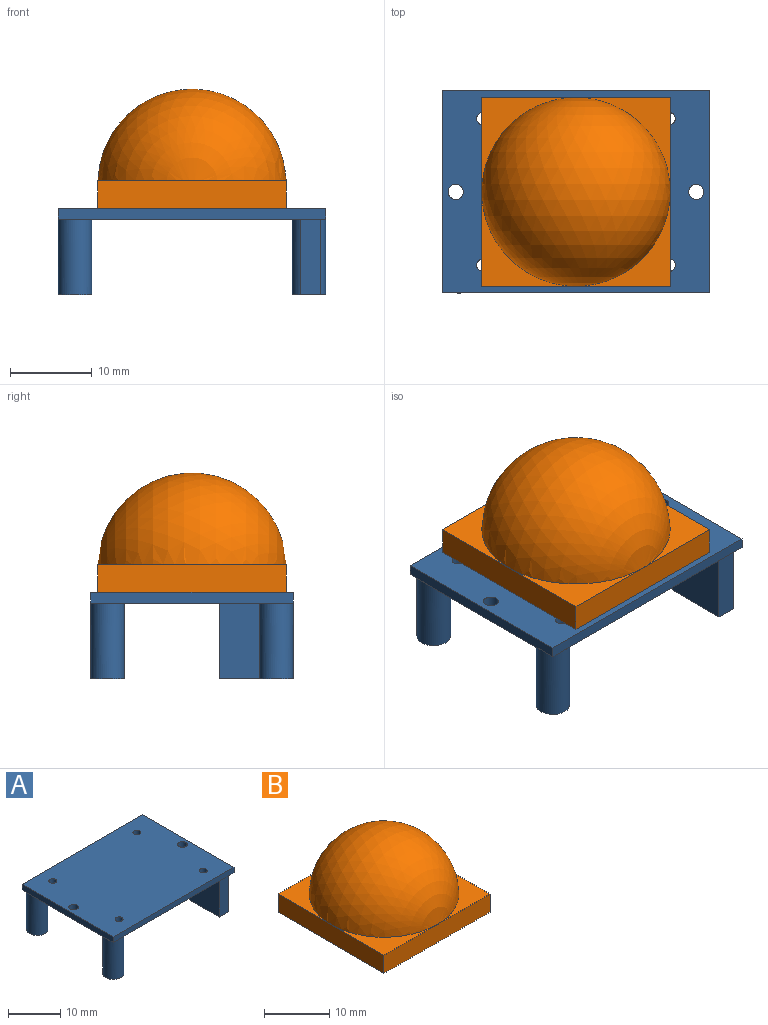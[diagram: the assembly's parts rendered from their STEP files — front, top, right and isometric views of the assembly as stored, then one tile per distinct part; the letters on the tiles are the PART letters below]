
ASSEMBLY  parts=2 mates=1
PART A: 26 faces, bbox 32.6x24.7x10.5 mm
  f0: plane 32.64x24.66mm, normal (0,0,-1), area 730mm2, adj f4,f5,f6,f7,f8,f9,f10,f11
  f1: plane 2.05x2.05mm, normal (0,0,-1), area 0.9mm2, adj f5,f6,f19
  f2: plane 2.05x2.05mm, normal (0,0,-1), area 0.9mm2, adj f6,f13,f17
  f3: plane 2.05x2.05mm, normal (0,0,-1), area 0.9mm2, adj f4,f13,f15
  f4: plane 32.64x1.3mm, normal (0,-1,0), area 42.4mm2, adj f0,f3,f5,f13,f14
  f5: plane 24.66x1.3mm, normal (1,0,0), area 32.1mm2, adj f0,f1,f4,f6,f14
  f6: plane 32.64x1.3mm, normal (0,1,0), area 42.4mm2, adj f0,f1,f2,f5,f13,f14
  f7: cylinder r=0.76mm len=1.52mm, axis (0,0,-1), area 6.2mm2, adj f0,f14
  f8: cylinder r=0.76mm len=1.52mm, axis (0,0,-1), area 6.2mm2, adj f0,f14
  f9: cylinder r=0.76mm len=1.52mm, axis (0,0,-1), area 6.2mm2, adj f0,f14
  f10: cylinder r=0.76mm len=1.52mm, axis (0,0,-1), area 6.2mm2, adj f0,f14
  f11: cylinder r=0.93mm len=1.85mm, axis (0,0,-1), area 7.6mm2, adj f0,f14
  f12: cylinder r=0.93mm len=1.85mm, axis (0,0,-1), area 7.6mm2, adj f0,f14
  f13: plane 24.66x1.3mm, normal (-1,0,0), area 32.1mm2, adj f0,f2,f3,f4,f6,f14
  f14: plane 32.64x24.66mm, normal (0,0,1), area 792.3mm2, adj f4,f5,f6,f7,f8,f9,f10,f11
  f15: cylinder r=2.05mm len=9.22mm, axis (0,0,1), area 118.8mm2, adj f0,f3,f16
  f16: plane 4.1x4.1mm, normal (0,0,-1), area 13.2mm2, adj f15
  f17: cylinder r=2.05mm len=9.22mm, axis (0,0,1), area 118.8mm2, adj f0,f2,f18
  f18: plane 4.1x4.1mm, normal (0,0,-1), area 13.2mm2, adj f17
  f19: cylinder r=2.05mm len=9.22mm, axis (0,0,1), area 118.8mm2, adj f0,f1,f20
  f20: plane 4.1x4.1mm, normal (0,0,-1), area 13.2mm2, adj f19
  f21: plane 9.22x8.08mm, normal (-1,0,0), area 74.5mm2, adj f0,f22,f24,f25
  f22: plane 9.22x2.47mm, normal (0,1,0), area 22.8mm2, adj f0,f21,f23,f25
  f23: plane 9.22x8.08mm, normal (1,0,0), area 74.5mm2, adj f0,f22,f24,f25
  f24: plane 9.22x2.47mm, normal (0,-1,0), area 22.8mm2, adj f0,f21,f23,f25
  f25: plane 8.08x2.47mm, normal (0,0,-1), area 20mm2, adj f21,f22,f23,f24
PART B: 7 faces, bbox 23x23x19.6 mm
  f0: plane 23x3.39mm, normal (1,0,0), area 78mm2, adj f1,f3,f4,f5
  f1: plane 23x3.39mm, normal (0,1,0), area 78mm2, adj f0,f2,f4,f5
  f2: plane 23x3.39mm, normal (-1,0,0), area 78mm2, adj f1,f3,f4,f5
  f3: plane 23x3.39mm, normal (0,-1,0), area 78mm2, adj f0,f2,f4,f5
  f4: plane 23x23mm, normal (0,0,1), area 113.8mm2, adj f0,f1,f2,f3,f6
  f5: plane 23x23mm, normal (0,0,-1), area 529mm2, adj f0,f1,f2,f3
  f6: sphere r=11.5mm, area 809.5mm2, adj f4
PLACE A t=(0,0,-1.3)mm
PLACE B at identity
MATE fastened A.f14 <-> B.f5  axis (0,0,1) through (0,0,0)mm
